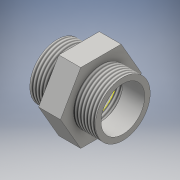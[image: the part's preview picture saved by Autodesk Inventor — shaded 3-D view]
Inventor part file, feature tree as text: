
AUTODESK INVENTOR PART (.ipt)
format: ipt  version: 2016 (Build 200138000, 138)  size: 137,216 bytes
history: native  units: mm
features: sketch x3, thread x3, extrude x2, mirror x1
ambient origin geometry x8: Origin, YZ Plane, XZ Plane, XY Plane, X Axis, Y Axis, Z Axis, Center Point
bodies: Solid1 (feature_tree)
feature tree (9):
  extrude  "Extrusion1"  Depth=40.0mm
  sketch  "Sketch3"  dims[d7=10.0mm d8=0.0mm d12=10.0mm d13=40.0mm d14=0.0mm d15=10.0mm d16=0.0mm]
  thread  "Thread1"  [1 undecoded]
  extrude  "Extrusion4"  Depth=10.0mm
  thread  "Thread2"  [1 undecoded]
  mirror  "Mirror1"
  thread  "Thread3"  [1 undecoded]
  sketch  "Sketch1"  dims[d0=100.0mm d1=64.0mm d2=40.0mm d3=0.0mm]
  sketch  "Sketch4"  dims[d17=10.0mm d18=0.0mm]
note: 3 required parameter values undecoded (feature->parameter linkage not recoverable at this tier; creation-order binding heuristic only, values carry confidence <= 0.55)
